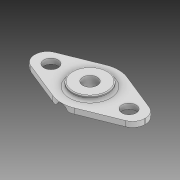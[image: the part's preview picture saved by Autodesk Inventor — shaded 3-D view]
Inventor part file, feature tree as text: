
AUTODESK INVENTOR PART (.ipt)
format: ipt  version: 2020 (Build 240168000, 168)  size: 316,416 bytes
history: native  units: mm
features: other x7, sketch x4, extrude x3, fillet x3, revolve x2, imported_body x1
ambient origin geometry x8: Origin, YZ Plane, XZ Plane, XY Plane, X Axis, Y Axis, Z Axis, Center Point
bodies: Solid1 (feature_tree)
feature tree (20):
  other  "HD_mastersketch.ipt"
  other  "Blocks"
  revolve  "Revolution1"  [1 undecoded]
  extrude  "Extrusion1"  Depth=10.0mm
  extrude  "Extrusion2"  TaperAngle=0.0deg  [1 undecoded]
  fillet  "Fillet1"  [1 undecoded]
  extrude  "Extrusion3"  Depth=1.0mm
  revolve  "Revolution2"  [1 undecoded]
  fillet  "Fillet3"  Radius=5.7mm
  fillet  "Fillet4"  Radius=5.7mm
  other  "608 bearing"
  other  "Belt"
  other  "Rotor"
  imported_body  "Base"
  sketch  "Sketch8"  dims[d1=10.0mm d24=7.0mm d25=22.0mm d26=8.0mm]
  sketch  "Sketch9"  dims[d2=90.0deg d3=5.0mm d4=10.0mm]
  sketch  "Sketch10"  dims[d5=15.0mm d6=0.0mm d7=0.0mm d8=0.0mm d9=0.0mm]
  sketch  "Sketch14"  dims[d10=7.0mm d11=3.6mm d12=2.3mm d13=5.7mm d14=5.7mm d15=0.0mm d29=1.65mm d30=3.0mm d32=10.0mm d33=1.5mm d34=90.0deg d36=4.0mm d37=2.0mm d38=1.0mm]
  other  "608 bearing:1"
  other  "608 bearing:2"
note: 4 required parameter values undecoded (feature->parameter linkage not recoverable at this tier; creation-order binding heuristic only, values carry confidence <= 0.55)